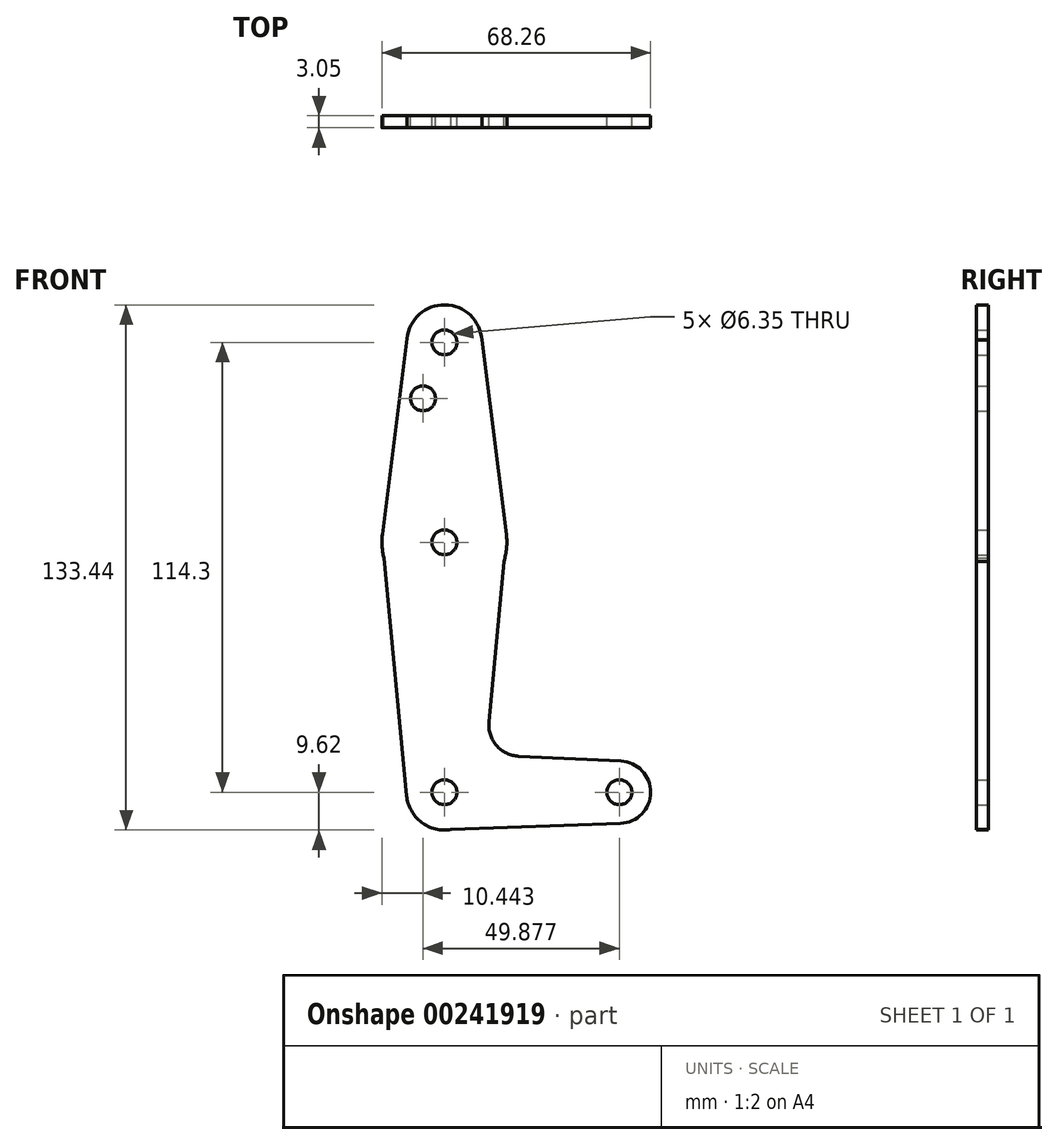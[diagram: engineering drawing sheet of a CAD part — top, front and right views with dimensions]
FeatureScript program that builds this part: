
annotation { "Feature Type Name" : "Feature", "Feature Type Description" : "" }
export const myFeature = defineFeature(function(context is Context, id is Id, definition is map)
    precondition{}
    {
        {
            var Q0;
            Q0=qCreatedBy(makeId("Front.planeOp"),FACE);
            var sketch = newSketch(context, id + "F0", { "sketchPlane" : qUnion([Q0])});
            skCircle(sketch, "E0", {"center": v(-29.04, 50.8) * mm, "radius": 9.53 * mm});
            skCircle(sketch, "E1", {"center": v(-29.04, 0) * mm, "radius": 15.88 * mm});
            skCircle(sketch, "E2", {"center": v(-29.04, -63.5) * mm, "radius": 9.62 * mm});
            skLineSegment(sketch, "E3", {"start": v(-29.04, -63.5) * mm, "end": v(15.41, -63.5) * mm, "construction": true});
            skCircle(sketch, "E4", {"center": v(15.41, -63.5) * mm, "radius": 7.94 * mm});
            skLineSegment(sketch, "E5", {"start": v(-29.04, 50.8) * mm, "end": v(-29.04, 0) * mm, "construction": true});
            skLineSegment(sketch, "E6", {"start": v(-29.04, 0) * mm, "end": v(-29.04, -63.5) * mm, "construction": true});
            skLineSegment(sketch, "E7", {"start": v(-38.52, 51.75) * mm, "end": v(-44.8, 1.99) * mm});
            skLineSegment(sketch, "E8", {"start": v(-44.8, 1.99) * mm, "end": v(-44.8, 0) * mm});
            skLineSegment(sketch, "E9", {"start": v(-44.8, 0) * mm, "end": v(-38.62, -64.42) * mm});
            skLineSegment(sketch, "E10", {"start": v(-19.53, 51.38) * mm, "end": v(-13.29, 1.99) * mm});
            skLineSegment(sketch, "E11", {"start": v(-13.29, 1.99) * mm, "end": v(-17.72, -45.67) * mm});
            skLineSegment(sketch, "E12", {"start": v(-10.18, -54.35) * mm, "end": v(15.78, -55.57) * mm});
            skLineSegment(sketch, "E13", {"start": v(-30.03, -73.07) * mm, "end": v(15.7, -71.43) * mm});
            skCircle(sketch, "E14", {"center": v(-29.04, 50.8) * mm, "radius": 3.18 * mm});
            skCircle(sketch, "E15", {"center": v(-29.04, -63.5) * mm, "radius": 3.18 * mm});
            skCircle(sketch, "E16", {"center": v(15.41, -63.5) * mm, "radius": 3.18 * mm});
            skCircle(sketch, "E17", {"center": v(-29.04, 0) * mm, "radius": 3.18 * mm});
            skCircle(sketch, "E18", {"center": v(-34.47, 36.57) * mm, "radius": 3.18 * mm});
            skPoint(sketch, "E19.newPointA", {"position": v(-19.46, -64.42) * mm});
            skArc(sketch, "E19.filletArc", {"start": v(-17.72, -45.67) * mm, "mid": v(-15.8, -51.62) * mm, "end": v(-10.18, -54.35) * mm});
            skSolve(sketch);
        }
        {
            var Q0;
            Q0 = qSketchRegion(id + "F0", true);
            extrude(context, id + "F1", {"entities" : qUnion([Q0]), "depth" : 3.05 * mm});
        }
    });
